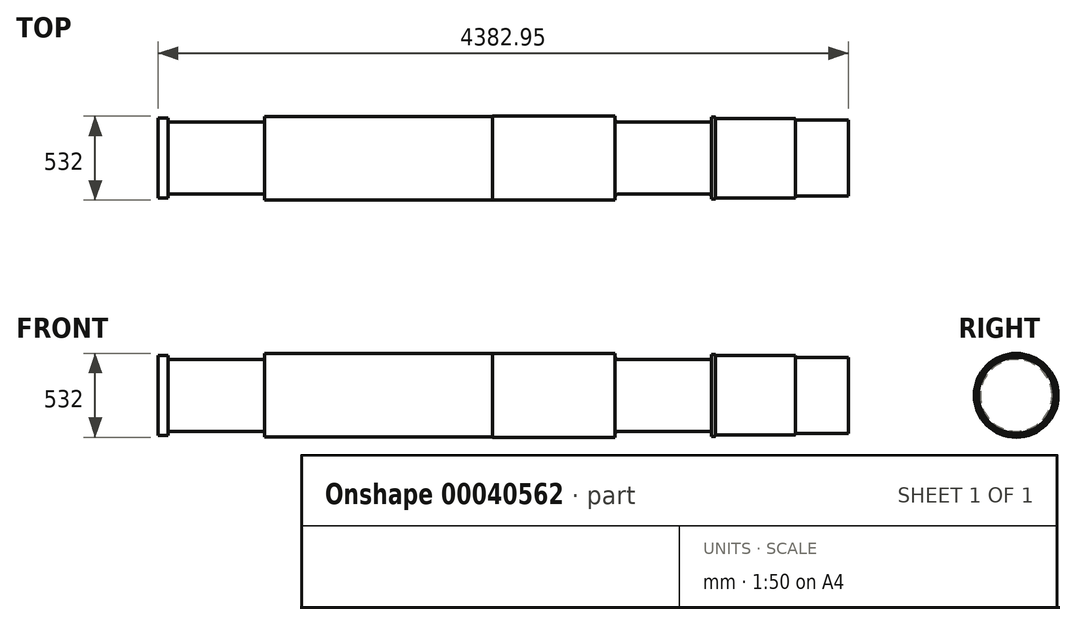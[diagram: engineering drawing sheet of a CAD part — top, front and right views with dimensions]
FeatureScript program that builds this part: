
annotation { "Feature Type Name" : "Feature", "Feature Type Description" : "" }
export const myFeature = defineFeature(function(context is Context, id is Id, definition is map)
    precondition{}
    {
        {
            var Q0;
            Q0=qCreatedBy(makeId("Front.planeOp"),FACE);
            var sketch = newSketch(context, id + "F0", { "sketchPlane" : qUnion([Q0])});
            skLineSegment(sketch, "E0", {"start": v(0, 0) * mm, "end": v(0, 101.6) * mm});
            skLineSegment(sketch, "E1", {"start": v(0, 101.6) * mm, "end": v(224, 101.6) * mm});
            skLineSegment(sketch, "E2", {"start": v(0, 0) * mm, "end": v(46415, 0) * mm});
            skLineSegment(sketch, "E3", {"start": v(259, 254) * mm, "end": v(321, 254) * mm});
            skLineSegment(sketch, "E4", {"start": v(321, 254) * mm, "end": v(321, 0) * mm});
            skPoint(sketch, "E5.visualSharp", {"position": v(254, 101.6) * mm});
            skArc(sketch, "E5.filletArc", {"start": v(224, 101.6) * mm, "mid": v(245.21, 110.39) * mm, "end": v(254, 131.6) * mm});
            skLineSegment(sketch, "E6", {"start": v(336, 228.6) * mm, "end": v(918.8, 228.6) * mm});
            skLineSegment(sketch, "E7", {"start": v(933.8, 265) * mm, "end": v(933.8, 0) * mm});
            skLineSegment(sketch, "E8", {"start": v(933.8, 265) * mm, "end": v(2380.8, 265) * mm});
            skPoint(sketch, "E9.visualSharp", {"position": v(321, 228.6) * mm});
            skArc(sketch, "E9.filletArc", {"start": v(321, 243.6) * mm, "mid": v(325.4, 233) * mm, "end": v(336, 228.6) * mm});
            skPoint(sketch, "E10.newPointA", {"position": v(933.8, 0) * mm});
            skPoint(sketch, "E10.newPointB", {"position": v(933.8, 228.6) * mm});
            skArc(sketch, "E10.filletArc", {"start": v(918.8, 228.6) * mm, "mid": v(929.4, 233) * mm, "end": v(933.8, 243.6) * mm});
            skLineSegment(sketch, "E11", {"start": v(2380.8, 265) * mm, "end": v(2380.8, 261) * mm});
            skLineSegment(sketch, "E12", {"start": v(2380.8, 266) * mm, "end": v(2380.8, 0) * mm});
            skLineSegment(sketch, "E13", {"start": v(2380.8, 266) * mm, "end": v(3160.8, 266) * mm});
            skLineSegment(sketch, "E14", {"start": v(3160.8, 266) * mm, "end": v(3160.8, 247.6) * mm});
            skLineSegment(sketch, "E15", {"start": v(3160.8, 247.6) * mm, "end": v(3160.8, 0) * mm});
            skLineSegment(sketch, "E16", {"start": v(3179.8, 228.6) * mm, "end": v(3754.6, 228.6) * mm});
            skPoint(sketch, "E17.visualSharp", {"position": v(3160.8, 228.6) * mm});
            skArc(sketch, "E17.filletArc", {"start": v(3160.8, 247.6) * mm, "mid": v(3166.36, 234.16) * mm, "end": v(3179.8, 228.6) * mm});
            skLineSegment(sketch, "E18", {"start": v(3773.6, 260.35) * mm, "end": v(3773.6, 0) * mm});
            skPoint(sketch, "E19.newPointA", {"position": v(3773.6, 228.6) * mm});
            skPoint(sketch, "E19.newPointB", {"position": v(3773.6, 0) * mm});
            skArc(sketch, "E19.filletArc", {"start": v(3754.6, 228.6) * mm, "mid": v(3768.04, 234.16) * mm, "end": v(3773.6, 247.6) * mm});
            skPoint(sketch, "E20.orphan", {"position": v(3773.6, 260.35) * mm});
            skLineSegment(sketch, "E21", {"start": v(3773.6, 260.35) * mm, "end": v(3799, 260.35) * mm});
            skLineSegment(sketch, "E22.0", {"start": v(3799, 255.22) * mm, "end": v(3799, 0) * mm});
            skLineSegment(sketch, "E23", {"start": v(3802, 252.22) * mm, "end": v(4305.4, 252.22) * mm});
            skPoint(sketch, "E24.visualSharp", {"position": v(3799, 252.22) * mm});
            skArc(sketch, "E24.filletArc", {"start": v(3799, 255.22) * mm, "mid": v(3799.88, 253.1) * mm, "end": v(3802, 252.22) * mm});
            skLineSegment(sketch, "E25", {"start": v(4313.4, 241.3) * mm, "end": v(4641.95, 241.3) * mm});
            skPoint(sketch, "E26.visualSharp", {"position": v(4305.4, 241.3) * mm});
            skArc(sketch, "E26.filletArc", {"start": v(4305.4, 249.3) * mm, "mid": v(4307.74, 243.64) * mm, "end": v(4313.4, 241.3) * mm});
            skLineSegment(sketch, "E27", {"start": v(4641.95, 241.3) * mm, "end": v(4641.95, 0) * mm});
            skLineSegment(sketch, "E28", {"start": v(3799, 260.35) * mm, "end": v(3799, 255.22) * mm});
            skLineSegment(sketch, "E29", {"start": v(259, 254) * mm, "end": v(259, 0) * mm});
            skLineSegment(sketch, "E30", {"start": v(4305.4, 252.22) * mm, "end": v(4305.4, 0) * mm});
            skSolve(sketch);
        }
        {
            var Q0;
            {var subQ0=sQuery(id+"F0.wireOp",EDGE,"E0");Q0=makeQuery(id+"F0.imprint","IMPRINT",FACE,{"disambiguationData":[TD([[makeQuery(id+"F0.imprint","IMPRINT",EDGE,{"derivedFrom":subQ0}),-1.0]])]});}
            var Q1;
            {var subQ5=sQuery(id+"F0.wireOp",EDGE,"E3");Q1=makeQuery(id+"F0.imprint","IMPRINT",FACE,{"disambiguationData":[TD([[makeQuery(id+"F0.imprint","IMPRINT",EDGE,{"derivedFrom":subQ5}),-1.0]])]});}
            var Q2;
            {var subQ4=sQuery(id+"F0.wireOp",EDGE,"9d2fc1d8-7ba8-4194-b406-f62aabbba51c");Q2=makeQuery(id+"F0.imprint","IMPRINT",FACE,{"disambiguationData":[TD([[makeQuery(id+"F0.imprint","IMPRINT",EDGE,{"derivedFrom":subQ4}),1.0]])]});}
            var Q3;
            {var subQ2=sQuery(id+"F0.wireOp",EDGE,"E8");Q3=makeQuery(id+"F0.imprint","IMPRINT",FACE,{"disambiguationData":[TD([[makeQuery(id+"F0.imprint","IMPRINT",EDGE,{"derivedFrom":subQ2}),-1.0]])]});}
            var Q4;
            {var subQ1=sQuery(id+"F0.wireOp",EDGE,"E13");Q4=makeQuery(id+"F0.imprint","IMPRINT",FACE,{"disambiguationData":[TD([[makeQuery(id+"F0.imprint","IMPRINT",EDGE,{"derivedFrom":subQ1}),-1.0]])]});}
            var Q5;
            {var subQ3=sQuery(id+"F0.wireOp",EDGE,"E15");Q5=makeQuery(id+"F0.imprint","IMPRINT",FACE,{"disambiguationData":[TD([[makeQuery(id+"F0.imprint","IMPRINT",EDGE,{"derivedFrom":subQ3}),1.0]])]});}
            var Q6;
            {var subQ4=sQuery(id+"F0.wireOp",EDGE,"E22.0");Q6=makeQuery(id+"F0.imprint","IMPRINT",FACE,{"disambiguationData":[TD([[makeQuery(id+"F0.imprint","IMPRINT",EDGE,{"derivedFrom":subQ4}),1.0]])]});}
            var Q7;
            {var subQ3=sQuery(id+"F0.wireOp",EDGE,"E21");Q7=makeQuery(id+"F0.imprint","IMPRINT",FACE,{"disambiguationData":[TD([[makeQuery(id+"F0.imprint","IMPRINT",EDGE,{"derivedFrom":subQ3}),-1.0]])]});}
            var Q8;
            Q8=makeQuery(id+"F0.imprint","IMPRINT",FACE,{"disambiguationData":[TD([[makeQuery(id+"F0.imprint","IMPRINT",EDGE,{"derivedFrom":sQuery(id+"F0.wireOp",EDGE,"E25")}),-1.0]])]});
            var Q9;
            Q9=makeQuery(id+"F0.imprint","IMPRINT",FACE,{"disambiguationData":[TD([[makeQuery(id+"F0.imprint","IMPRINT",EDGE,{"derivedFrom":sQuery(id+"F0.wireOp",EDGE,"E6")}),-1.0]])]});
            var Q10;
            Q10=sQuery(id+"F0.wireOp",EDGE,"E2");
            revolve(context, id + "F1", {"entities" : qUnion([Q0, Q1, Q2, Q3, Q4, Q5, Q6, Q7, Q8, Q9]), "axis" : qUnion([Q10]), "revolveType" : RevolveType.FULL});
        }
        {
            var Q0;
            Q0=makeQuery(id+"F1.opRevolve","SWEPT_BODY",BODY,{"disambiguationData":[OSD([sQuery(id+"F0.wireOp",EDGE,"E2"),sQuery(id+"F0.wireOp",EDGE,"E3"),sQuery(id+"F0.wireOp",EDGE,"E4"),sQuery(id+"F0.wireOp",EDGE,"E6"),sQuery(id+"F0.wireOp",EDGE,"E7"),sQuery(id+"F0.wireOp",EDGE,"E8"),sQuery(id+"F0.wireOp",EDGE,"E9.filletArc"),sQuery(id+"F0.wireOp",EDGE,"E10.filletArc"),sQuery(id+"F0.wireOp",EDGE,"E12"),sQuery(id+"F0.wireOp",EDGE,"E13"),sQuery(id+"F0.wireOp",EDGE,"E14"),sQuery(id+"F0.wireOp",EDGE,"E16"),sQuery(id+"F0.wireOp",EDGE,"E17.filletArc"),sQuery(id+"F0.wireOp",EDGE,"E18"),sQuery(id+"F0.wireOp",EDGE,"E19.filletArc"),sQuery(id+"F0.wireOp",EDGE,"E21"),sQuery(id+"F0.wireOp",EDGE,"E23"),sQuery(id+"F0.wireOp",EDGE,"E24.filletArc"),sQuery(id+"F0.wireOp",EDGE,"E25"),sQuery(id+"F0.wireOp",EDGE,"E26.filletArc"),sQuery(id+"F0.wireOp",EDGE,"E27"),sQuery(id+"F0.wireOp",EDGE,"E28"),sQuery(id+"F0.wireOp",EDGE,"E29"),sQuery(id+"F0.wireOp",EDGE,"E30")])]});
            transform(context, id + "F2", {"entities" : qUnion([Q0]), "transformType" : TransformType.TRANSLATION_3D, "dx" : 0 * mm, "dy" : 0 * mm, "dz" : 862.5 * mm, "makeCopy" : false});
        }
    });
